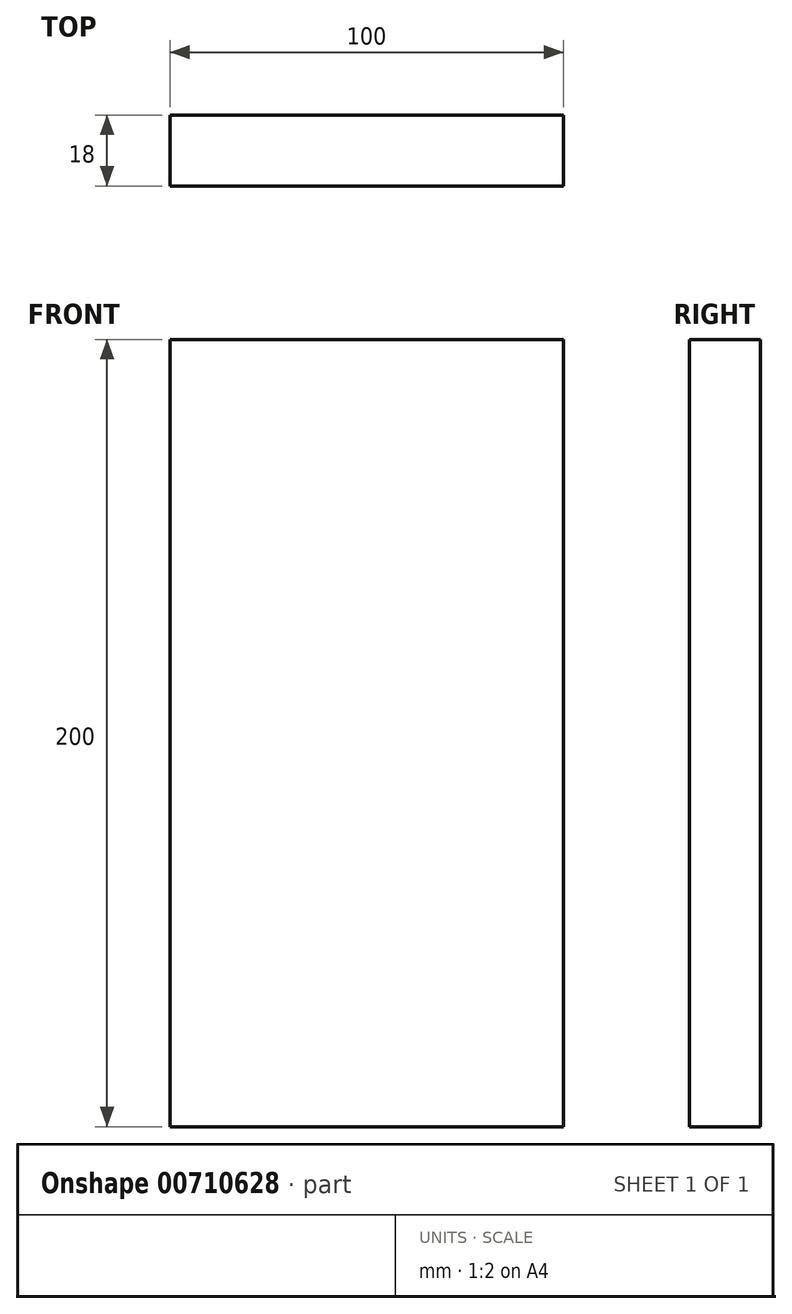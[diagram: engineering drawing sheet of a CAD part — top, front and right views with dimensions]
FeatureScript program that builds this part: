
annotation { "Feature Type Name" : "Feature", "Feature Type Description" : "" }
export const myFeature = defineFeature(function(context is Context, id is Id, definition is map)
    precondition{}
    {
        {
            var Q0;
            Q0=qCreatedBy(makeId("Front.planeOp"),FACE);
            var sketch = newSketch(context, id + "F0", { "sketchPlane" : qUnion([Q0])});
            skLineSegment(sketch, "E0.bottom", {"start": v(0, 0) * mm, "end": v(100, 0) * mm});
            skLineSegment(sketch, "E0.top", {"start": v(0, 200) * mm, "end": v(100, 200) * mm});
            skLineSegment(sketch, "E0.left", {"start": v(0, 0) * mm, "end": v(0, 200) * mm});
            skLineSegment(sketch, "E0.right", {"start": v(100, 0) * mm, "end": v(100, 200) * mm});
            skSolve(sketch);
        }
        {
            var Q0;
            Q0=makeQuery(id+"F0.imprint","IMPRINT",FACE,{"disambiguationData":[TD([[makeQuery(id+"F0.imprint","IMPRINT",EDGE,{"derivedFrom":sQuery(id+"F0.wireOp",EDGE,"E0.bottom")}),1.0]])]});
            extrude(context, id + "F1", {"entities" : qUnion([Q0]), "depth" : 18 * mm, "offsetDistance" : 25 * mm});
        }
    });
